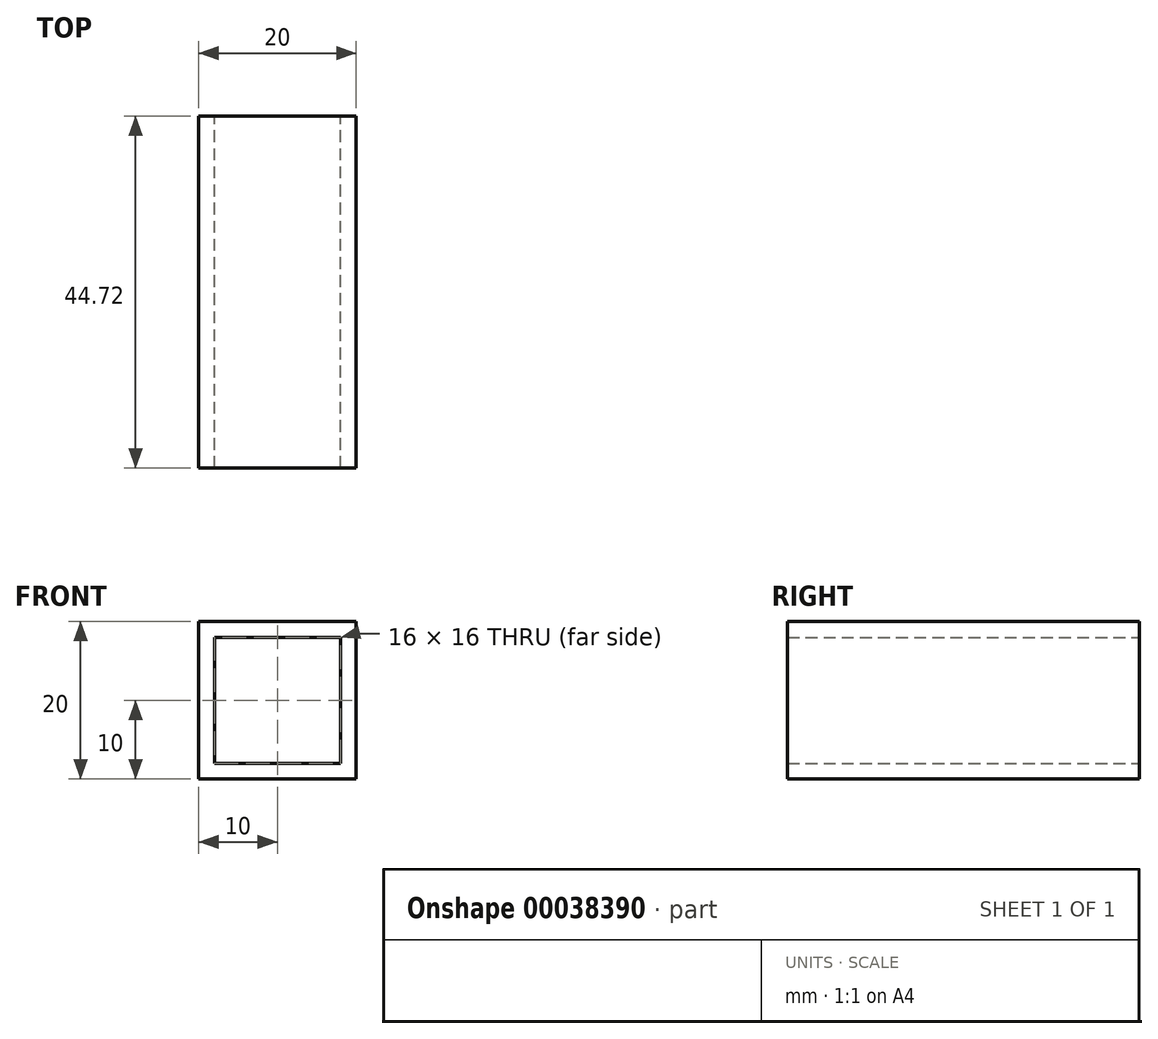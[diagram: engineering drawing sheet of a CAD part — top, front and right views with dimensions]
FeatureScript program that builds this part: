
annotation { "Feature Type Name" : "Feature", "Feature Type Description" : "" }
export const myFeature = defineFeature(function(context is Context, id is Id, definition is map)
    precondition{}
    {
        {
            var Q0;
            Q0=qCreatedBy(makeId("Front.planeOp"),FACE);
            var sketch = newSketch(context, id + "F0", { "sketchPlane" : qUnion([Q0])});
            skLineSegment(sketch, "E0.bottom", {"start": v(-20, 20) * mm, "end": v(0, 20) * mm});
            skLineSegment(sketch, "E0.top", {"start": v(-20, 0) * mm, "end": v(0, 0) * mm});
            skLineSegment(sketch, "E0.left", {"start": v(-20, 20) * mm, "end": v(-20, 0) * mm});
            skLineSegment(sketch, "E0.right", {"start": v(0, 20) * mm, "end": v(0, 0) * mm});
            skLineSegment(sketch, "E1.0", {"start": v(-18, 2) * mm, "end": v(-2, 2) * mm});
            skLineSegment(sketch, "E1.1", {"start": v(-18, 18) * mm, "end": v(-18, 2) * mm});
            skLineSegment(sketch, "E1.2", {"start": v(-18, 18) * mm, "end": v(-2, 18) * mm});
            skLineSegment(sketch, "E1.3", {"start": v(-2, 18) * mm, "end": v(-2, 2) * mm});
            skSolve(sketch);
        }
        {
            var Q0;
            Q0=makeQuery(id+"F0.imprint","IMPRINT",FACE,{"disambiguationData":[TD([[makeQuery(id+"F0.imprint","IMPRINT",EDGE,{"derivedFrom":sQuery(id+"F0.wireOp",EDGE,"E0.bottom")}),-1.0]])]});
            extrude(context, id + "F1", {"entities" : qUnion([Q0]), "depth" : 44.72 * mm});
        }
    });
